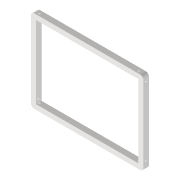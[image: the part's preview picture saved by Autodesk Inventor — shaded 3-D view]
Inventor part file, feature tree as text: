
AUTODESK INVENTOR PART (.ipt)
format: ipt  version: 2022 (Build 260153000, 153)  size: 151,040 bytes
history: native  units: mm
features: extrude x5, sketch x5, reference x3, other x2
ambient origin geometry x8: Origin, YZ Plane, XZ Plane, XY Plane, X Axis, Y Axis, Z Axis, Center Point
bodies: Volumenkörper1 (feature_tree)
feature tree (15):
  extrude  "Extrusion1"  TaperAngle=0.0deg  [1 undecoded]
  extrude  "Extrusion3"  Depth=2.8mm
  extrude  "Extrusion4"  Depth=20.0mm TaperAngle=0.0deg
  extrude  "Extrusion5"  Depth=2.8mm
  extrude  "Extrusion6"  Depth=5.0mm TaperAngle=0.0deg
  sketch  "Skizze1"  dims[d3=5.0mm d5=0.0mm]
  sketch  "Skizze4"  dims[d28=2.8mm d30=2.8mm]
  reference  "Referenz4"
  sketch  "Skizze5"  dims[d31=20.0mm d32=0.0mm d33=20.0mm d34=0.0mm]
  sketch  "Skizze6"  dims[d35=2.8mm d37=2.8mm]
  reference  "Referenz5"
  reference  "Referenz6"
  sketch  "Skizze7"  dims[d38=20.0mm d39=0.0mm d40=20.0mm d41=0.0mm d42=158.842mm d43=116.8304mm d45=7.0mm d46=7.0mm d47=7.0mm d48=7.0mm d49=5.0mm d50=5.0mm]
  other  "Omnicscope_Xiao.iam"
  other  "Omniscope_USBC_Base:1"
note: 1 required parameter value undecoded (feature->parameter linkage not recoverable at this tier; creation-order binding heuristic only, values carry confidence <= 0.55)
